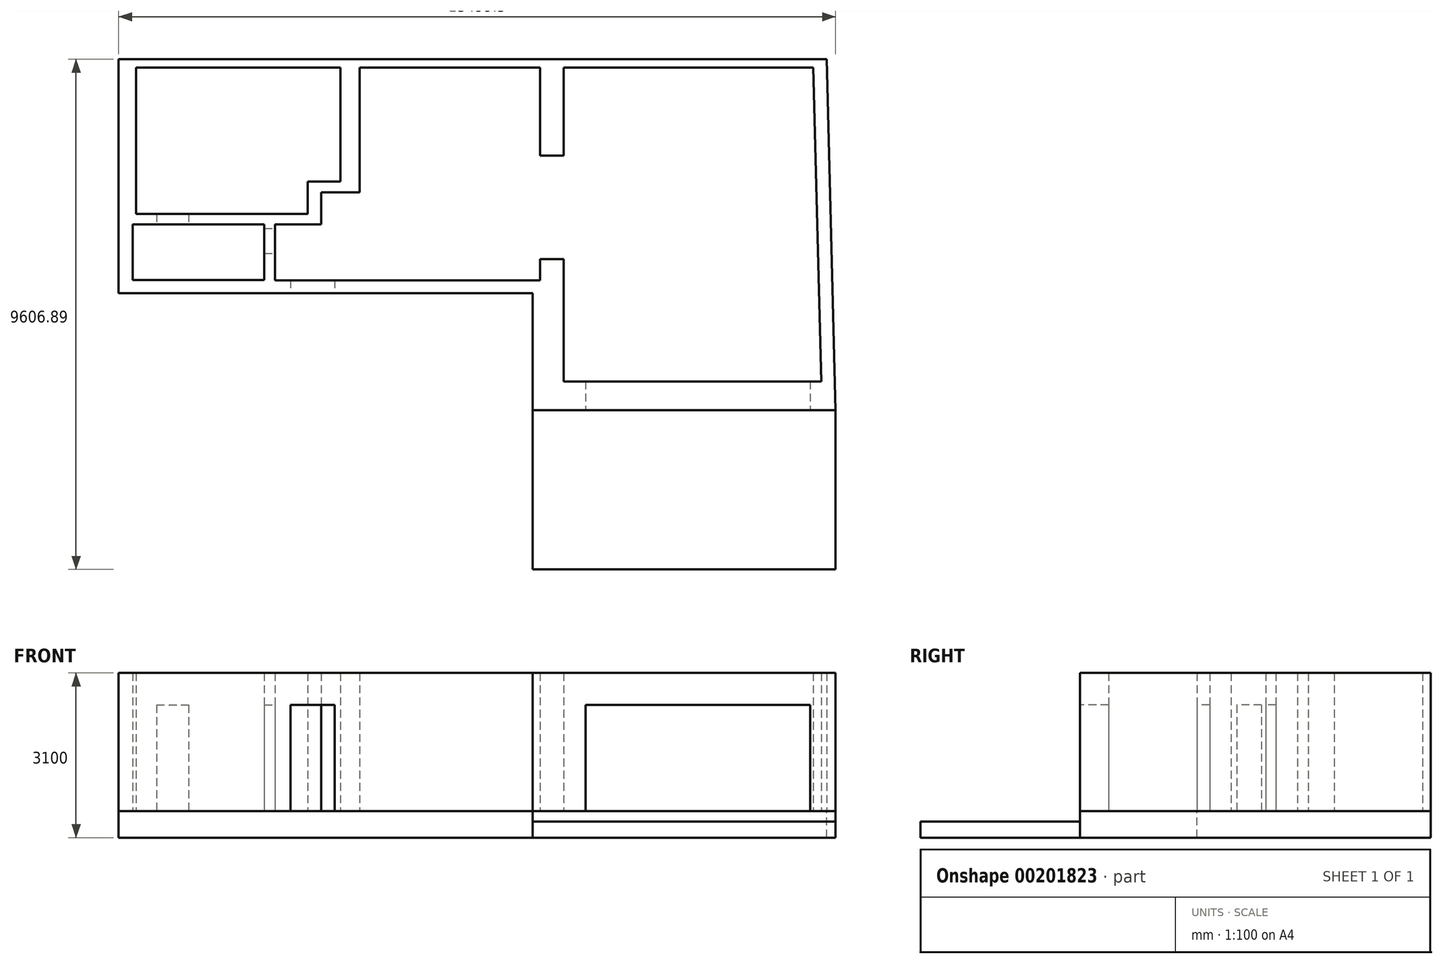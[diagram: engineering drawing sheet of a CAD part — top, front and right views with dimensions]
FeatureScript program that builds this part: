
annotation { "Feature Type Name" : "Feature", "Feature Type Description" : "" }
export const myFeature = defineFeature(function(context is Context, id is Id, definition is map)
    precondition{}
    {
        {
            var Q0;
            Q0=qCreatedBy(makeId("Top.planeOp"),FACE);
            var sketch = newSketch(context, id + "F0", { "sketchPlane" : qUnion([Q0])});
            skLineSegment(sketch, "E0", {"start": v(-2393.35, -759.16) * mm, "end": v(-2393.35, -518.36) * mm});
            skLineSegment(sketch, "E1", {"start": v(-2393.35, -518.36) * mm, "end": v(-2688.76, -518.36) * mm});
            skLineSegment(sketch, "E2", {"start": v(-2688.76, -518.36) * mm, "end": v(-2688.76, -9.52) * mm});
            skLineSegment(sketch, "E3", {"start": v(-2688.76, -9.52) * mm, "end": v(-2888.42, -9.52) * mm});
            skLineSegment(sketch, "E4", {"start": v(-2888.42, -9.52) * mm, "end": v(-2888.42, -513.76) * mm});
            skLineSegment(sketch, "E5", {"start": v(-2888.42, -513.76) * mm, "end": v(-5364.36, -513.76) * mm});
            skLineSegment(sketch, "E6", {"start": v(-5364.36, -513.76) * mm, "end": v(-5364.36, 536.6) * mm});
            skLineSegment(sketch, "E7", {"start": v(-5364.36, 536.6) * mm, "end": v(-4917.07, 536.6) * mm});
            skLineSegment(sketch, "E8", {"start": v(-4917.07, 536.6) * mm, "end": v(-4917.07, 728.5) * mm});
            skLineSegment(sketch, "E9", {"start": v(-4917.07, 728.5) * mm, "end": v(-5303.89, 728.5) * mm});
            skLineSegment(sketch, "E10", {"start": v(-5303.89, 728.5) * mm, "end": v(-5303.89, 3488.5) * mm});
            skLineSegment(sketch, "E11", {"start": v(-5303.89, 3488.5) * mm, "end": v(-1453.89, 3488.5) * mm});
            skLineSegment(sketch, "E12", {"start": v(-1453.89, 3488.5) * mm, "end": v(-1453.89, 1338.5) * mm});
            skLineSegment(sketch, "E13", {"start": v(-1453.89, 1338.5) * mm, "end": v(-2073.89, 1338.5) * mm});
            skLineSegment(sketch, "E14", {"start": v(-2073.89, 1338.5) * mm, "end": v(-2073.89, 728.5) * mm});
            skLineSegment(sketch, "E15", {"start": v(-2073.89, 728.5) * mm, "end": v(-4310.98, 728.5) * mm});
            skLineSegment(sketch, "E16", {"start": v(-4310.98, 728.5) * mm, "end": v(-4310.98, 536.6) * mm});
            skLineSegment(sketch, "E17", {"start": v(-4310.98, 536.6) * mm, "end": v(-2888.42, 536.6) * mm});
            skLineSegment(sketch, "E18", {"start": v(-2888.42, 536.6) * mm, "end": v(-2888.42, 458.15) * mm});
            skLineSegment(sketch, "E19", {"start": v(-2888.42, 458.15) * mm, "end": v(-2688.76, 458.15) * mm});
            skLineSegment(sketch, "E20", {"start": v(-2688.76, 458.15) * mm, "end": v(-2688.76, 536.6) * mm});
            skLineSegment(sketch, "E21", {"start": v(-2688.76, 536.6) * mm, "end": v(-1818.64, 536.6) * mm});
            skLineSegment(sketch, "E22", {"start": v(-1818.64, 536.6) * mm, "end": v(-1818.64, 1136.91) * mm});
            skLineSegment(sketch, "E23", {"start": v(-1818.64, 1136.91) * mm, "end": v(-1095.24, 1136.91) * mm});
            skLineSegment(sketch, "E24", {"start": v(-1095.24, 1136.91) * mm, "end": v(-1095.24, 3488.5) * mm});
            skLineSegment(sketch, "E25", {"start": v(-1095.24, 3488.5) * mm, "end": v(2304.76, 3488.5) * mm});
            skLineSegment(sketch, "E26", {"start": v(2304.76, 3488.5) * mm, "end": v(2304.76, 1828.5) * mm});
            skLineSegment(sketch, "E27", {"start": v(2304.76, 1828.5) * mm, "end": v(2749.76, 1828.5) * mm});
            skLineSegment(sketch, "E28", {"start": v(2749.76, 1828.5) * mm, "end": v(2749.76, 3488.5) * mm});
            skLineSegment(sketch, "E29", {"start": v(2749.76, 3488.5) * mm, "end": v(7449.76, 3488.5) * mm});
            skLineSegment(sketch, "E30", {"start": v(7449.76, 3488.5) * mm, "end": v(7599.76, -2422.42) * mm});
            skLineSegment(sketch, "E31", {"start": v(7599.76, -2422.42) * mm, "end": v(7390.63, -2422.42) * mm});
            skLineSegment(sketch, "E32", {"start": v(7390.63, -2422.42) * mm, "end": v(7390.63, -2963.9) * mm});
            skLineSegment(sketch, "E33", {"start": v(7390.63, -2963.9) * mm, "end": v(7867.99, -2963.9) * mm});
            skLineSegment(sketch, "E34", {"start": v(7700.33, 3642.99) * mm, "end": v(-5631.55, 3642.99) * mm});
            skLineSegment(sketch, "E35", {"start": v(-5631.55, 3642.99) * mm, "end": v(-5631.55, -759.16) * mm});
            skLineSegment(sketch, "E36", {"start": v(-5631.55, -759.16) * mm, "end": v(-2393.35, -759.16) * mm});
            skLineSegment(sketch, "E37", {"start": v(-1562.73, -759.16) * mm, "end": v(-1562.73, -518.36) * mm});
            skLineSegment(sketch, "E38", {"start": v(-1562.73, -518.36) * mm, "end": v(2304.76, -518.36) * mm});
            skLineSegment(sketch, "E39", {"start": v(2304.76, -518.36) * mm, "end": v(2304.76, -118.36) * mm});
            skLineSegment(sketch, "E40", {"start": v(2304.76, -118.36) * mm, "end": v(2749.76, -118.36) * mm});
            skLineSegment(sketch, "E41", {"start": v(2749.76, -118.36) * mm, "end": v(2749.76, -2422.42) * mm});
            skLineSegment(sketch, "E42", {"start": v(2749.76, -2422.42) * mm, "end": v(3164.2, -2422.42) * mm});
            skLineSegment(sketch, "E43", {"start": v(3164.2, -2422.42) * mm, "end": v(3164.2, -2963.9) * mm});
            skLineSegment(sketch, "E44", {"start": v(3164.2, -2963.9) * mm, "end": v(2166.9, -2963.9) * mm});
            skLineSegment(sketch, "E45", {"start": v(2166.9, -2963.9) * mm, "end": v(2166.9, -759.16) * mm});
            skLineSegment(sketch, "E46", {"start": v(2166.9, -759.16) * mm, "end": v(-1562.73, -759.16) * mm});
            skLineSegment(sketch, "E47", {"start": v(3164.2, -2422.42) * mm, "end": v(7390.63, -2422.42) * mm});
            skLineSegment(sketch, "E48", {"start": v(7390.63, -2963.9) * mm, "end": v(3164.2, -2963.9) * mm});
            skLineSegment(sketch, "E49", {"start": v(-2393.35, -518.36) * mm, "end": v(-1562.73, -518.36) * mm});
            skLineSegment(sketch, "E50", {"start": v(-1562.73, -759.16) * mm, "end": v(-2393.35, -759.16) * mm});
            skLineSegment(sketch, "E51", {"start": v(-2888.42, 458.15) * mm, "end": v(-2888.42, -9.52) * mm});
            skLineSegment(sketch, "E52", {"start": v(-2688.76, -9.52) * mm, "end": v(-2688.76, 458.15) * mm});
            skLineSegment(sketch, "E53", {"start": v(-4917.07, 728.5) * mm, "end": v(-4310.98, 728.5) * mm});
            skLineSegment(sketch, "E54", {"start": v(-4310.98, 536.6) * mm, "end": v(-4917.07, 536.6) * mm});
            skLineSegment(sketch, "E55", {"start": v(-1453.89, 3488.5) * mm, "end": v(-1095.24, 3488.5) * mm, "construction": true});
            skLineSegment(sketch, "E56", {"start": v(-2888.42, 536.6) * mm, "end": v(-2688.76, 536.6) * mm, "construction": true});
            skLineSegment(sketch, "E57.bottom", {"start": v(-1095.24, 1136.91) * mm, "end": v(-1494.07, 1136.91) * mm});
            skLineSegment(sketch, "E58", {"start": v(2749.76, -118.36) * mm, "end": v(2749.76, 1828.5) * mm, "construction": true});
            skLineSegment(sketch, "E59", {"start": v(7700.33, 3642.99) * mm, "end": v(7867.99, -2963.9) * mm});
            skSolve(sketch);
        }
        {
            var Q0;
            Q0=makeQuery(id+"F0.imprint","IMPRINT",FACE,{"disambiguationData":[TD([[makeQuery(id+"F0.imprint","IMPRINT",EDGE,{"derivedFrom":sQuery(id+"F0.wireOp",EDGE,"E0")}),1.0]])]});
            var Q1;
            Q1=makeQuery(id+"F0.imprint","IMPRINT",FACE,{"disambiguationData":[TD([[makeQuery(id+"F0.imprint","IMPRINT",EDGE,{"derivedFrom":sQuery(id+"F0.wireOp",EDGE,"E0")}),-1.0]])]});
            var Q2;
            Q2=makeQuery(id+"F0.imprint","IMPRINT",FACE,{"disambiguationData":[TD([[makeQuery(id+"F0.imprint","IMPRINT",EDGE,{"derivedFrom":sQuery(id+"F0.wireOp",EDGE,"E37")}),-1.0]])]});
            var Q3;
            Q3=makeQuery(id+"F0.imprint","IMPRINT",FACE,{"disambiguationData":[TD([[makeQuery(id+"F0.imprint","IMPRINT",EDGE,{"derivedFrom":sQuery(id+"F0.wireOp",EDGE,"E32")}),-1.0]])]});
            var Q4;
            Q4=makeQuery(id+"F0.imprint","IMPRINT",FACE,{"disambiguationData":[TD([[makeQuery(id+"F0.imprint","IMPRINT",EDGE,{"derivedFrom":sQuery(id+"F0.wireOp",EDGE,"E3")}),-1.0]])]});
            var Q5;
            Q5=makeQuery(id+"F0.imprint","IMPRINT",FACE,{"disambiguationData":[TD([[makeQuery(id+"F0.imprint","IMPRINT",EDGE,{"derivedFrom":sQuery(id+"F0.wireOp",EDGE,"E8")}),-1.0]])]});
            var Q6;
            Q6=makeQuery(id+"F0.imprint","IMPRINT",FACE,{"disambiguationData":[TD([[makeQuery(id+"F0.imprint","IMPRINT",EDGE,{"derivedFrom":sQuery(id+"F0.wireOp",EDGE,"E9")}),-1.0]])]});
            var Q7;
            Q7=makeQuery(id+"F0.imprint","IMPRINT",FACE,{"disambiguationData":[TD([[makeQuery(id+"F0.imprint","IMPRINT",EDGE,{"derivedFrom":sQuery(id+"F0.wireOp",EDGE,"E4")}),-1.0]])]});
            var Q8;
            Q8=makeQuery(id+"F0.imprint","IMPRINT",FACE,{"disambiguationData":[TD([[makeQuery(id+"F0.imprint","IMPRINT",EDGE,{"derivedFrom":sQuery(id+"F0.wireOp",EDGE,"E1")}),-1.0]])]});
            extrude(context, id + "F1", {"entities" : qUnion([Q0, Q1, Q2, Q3, Q4, Q5, Q6, Q7, Q8]), "oppositeDirection" : true, "depth" : 500 * mm});
        }
        {
            var Q0;
            Q0=makeQuery(id+"F0.imprint","IMPRINT",FACE,{"disambiguationData":[TD([[makeQuery(id+"F0.imprint","IMPRINT",EDGE,{"derivedFrom":sQuery(id+"F0.wireOp",EDGE,"E0")}),1.0]])]});
            var Q1;
            Q1=makeQuery(id+"F0.imprint","IMPRINT",FACE,{"disambiguationData":[TD([[makeQuery(id+"F0.imprint","IMPRINT",EDGE,{"derivedFrom":sQuery(id+"F0.wireOp",EDGE,"E37")}),-1.0]])]});
            extrude(context, id + "F2", {"entities" : qUnion([Q0, Q1]), "depth" : 2600 * mm});
        }
        {
            var Q0;
            Q0=makeQuery(id+"F1.opExtrude","CAP_FACE",FACE,{"disambiguationData":[OSD([sQuery(id+"F0.wireOp",EDGE,"E33"),sQuery(id+"F0.wireOp",EDGE,"nEtp4WkR-m3eL-wyIJ-Avfq-g6g80PU1rIS8"),sQuery(id+"F0.wireOp",EDGE,"E34"),sQuery(id+"F0.wireOp",EDGE,"E35"),sQuery(id+"F0.wireOp",EDGE,"E36"),sQuery(id+"F0.wireOp",EDGE,"E44"),sQuery(id+"F0.wireOp",EDGE,"E45"),sQuery(id+"F0.wireOp",EDGE,"E46"),sQuery(id+"F0.wireOp",EDGE,"E48"),sQuery(id+"F0.wireOp",EDGE,"E50")])],"isStart":true});
            cPlane(context, id + "F3", {"entities" : qUnion([Q0]), "cplaneType" : CPlaneType.OFFSET, "offset" : 2000 * mm, "width" : 150 * mm, "height" : 150 * mm});
        }
        {
            var Q0;
            Q0=qCreatedBy(id+"F3.planeOp",FACE);
            var sketch = newSketch(context, id + "F4", { "sketchPlane" : qUnion([Q0])});
            skLineSegment(sketch, "E60.bottom", {"start": v(-2393.35, -518.36) * mm, "end": v(-1562.73, -518.36) * mm});
            skLineSegment(sketch, "E60.top", {"start": v(-2393.35, -759.16) * mm, "end": v(-1562.73, -759.16) * mm});
            skLineSegment(sketch, "E60.left", {"start": v(-2393.35, -518.36) * mm, "end": v(-2393.35, -759.16) * mm});
            skLineSegment(sketch, "E60.right", {"start": v(-1562.73, -518.36) * mm, "end": v(-1562.73, -759.16) * mm});
            skLineSegment(sketch, "E61.bottom", {"start": v(-2888.42, 458.15) * mm, "end": v(-2688.76, 458.15) * mm});
            skLineSegment(sketch, "E61.top", {"start": v(-2888.42, -9.52) * mm, "end": v(-2688.76, -9.52) * mm});
            skLineSegment(sketch, "E61.left", {"start": v(-2888.42, 458.15) * mm, "end": v(-2888.42, -9.52) * mm});
            skLineSegment(sketch, "E61.right", {"start": v(-2688.76, 458.15) * mm, "end": v(-2688.76, -9.52) * mm});
            skLineSegment(sketch, "E62.bottom", {"start": v(-4917.07, 728.5) * mm, "end": v(-4310.98, 728.5) * mm});
            skLineSegment(sketch, "E62.top", {"start": v(-4917.07, 536.6) * mm, "end": v(-4310.98, 536.6) * mm});
            skLineSegment(sketch, "E62.left", {"start": v(-4917.07, 728.5) * mm, "end": v(-4917.07, 536.6) * mm});
            skLineSegment(sketch, "E62.right", {"start": v(-4310.98, 728.5) * mm, "end": v(-4310.98, 536.6) * mm});
            skLineSegment(sketch, "E63.bottom", {"start": v(3164.2, -2422.42) * mm, "end": v(7390.63, -2422.42) * mm});
            skLineSegment(sketch, "E63.top", {"start": v(3164.2, -2963.9) * mm, "end": v(7390.63, -2963.9) * mm});
            skLineSegment(sketch, "E63.left", {"start": v(3164.2, -2422.42) * mm, "end": v(3164.2, -2963.9) * mm});
            skLineSegment(sketch, "E63.right", {"start": v(7390.63, -2422.42) * mm, "end": v(7390.63, -2963.9) * mm});
            skSolve(sketch);
        }
        {
            var Q0;
            Q0=makeQuery(id+"F4.imprint","IMPRINT",FACE,{"disambiguationData":[TD([[makeQuery(id+"F4.imprint","IMPRINT",EDGE,{"derivedFrom":sQuery(id+"F4.wireOp",EDGE,"E60.bottom")}),-1.0]])]});
            var Q1;
            Q1=makeQuery(id+"F4.imprint","IMPRINT",FACE,{"disambiguationData":[TD([[makeQuery(id+"F4.imprint","IMPRINT",EDGE,{"derivedFrom":sQuery(id+"F4.wireOp",EDGE,"E62.bottom")}),-1.0]])]});
            var Q2;
            Q2=makeQuery(id+"F4.imprint","IMPRINT",FACE,{"disambiguationData":[TD([[makeQuery(id+"F4.imprint","IMPRINT",EDGE,{"derivedFrom":sQuery(id+"F4.wireOp",EDGE,"E61.bottom")}),-1.0]])]});
            var Q3;
            Q3=makeQuery(id+"F4.imprint","IMPRINT",FACE,{"disambiguationData":[TD([[makeQuery(id+"F4.imprint","IMPRINT",EDGE,{"derivedFrom":sQuery(id+"F4.wireOp",EDGE,"E63.bottom")}),-1.0]])]});
            var Q4;
            Q4=makeQuery(id+"F2.opExtrude","CAP_FACE",FACE,{"disambiguationData":[OSD([sQuery(id+"F0.wireOp",EDGE,"E37"),sQuery(id+"F0.wireOp",EDGE,"E38"),sQuery(id+"F0.wireOp",EDGE,"E39"),sQuery(id+"F0.wireOp",EDGE,"E40"),sQuery(id+"F0.wireOp",EDGE,"E41"),sQuery(id+"F0.wireOp",EDGE,"E42"),sQuery(id+"F0.wireOp",EDGE,"E43"),sQuery(id+"F0.wireOp",EDGE,"E44"),sQuery(id+"F0.wireOp",EDGE,"E45"),sQuery(id+"F0.wireOp",EDGE,"E46")])],"isStart":false});
            extrude(context, id + "F5", {"entities" : qUnion([Q0, Q1, Q2, Q3]), "operationType" : NewBodyOperationType.ADD, "endBound" : BoundingType.UP_TO_SURFACE, "endBoundEntityFace" : qUnion([Q4]), "depth" : 25 * mm});
        }
        {
            var Q0;
            {var subQ0=sQuery(id+"F0.wireOp",EDGE,"E44");var subQ1=sQuery(id+"F0.wireOp",EDGE,"E33");Q0=makeQuery(id+"F5.boolean.opBoolean","MERGE",FACE,{"derivedFrom":[makeQuery(id+"F2.boolean.opBoolean","MERGE",FACE,{"derivedFrom":[makeQuery(id+"F1.opExtrude","SWEPT_FACE",FACE,{"disambiguationData":[OSD([subQ1,subQ0,sQuery(id+"F0.wireOp",EDGE,"E48")])]}),makeQuery(id+"F2.opExtrude","SWEPT_FACE",FACE,{"disambiguationData":[OSD([subQ1])]}),makeQuery(id+"F2.opExtrude","SWEPT_FACE",FACE,{"disambiguationData":[OSD([subQ0])]})]}),makeQuery(id+"F5.opExtrude","SWEPT_FACE",FACE,{"disambiguationData":[OSD([sQuery(id+"F4.wireOp",EDGE,"E63.top")])]})]});}
            var sketch = newSketch(context, id + "F6", { "sketchPlane" : qUnion([Q0])});
            skLineSegment(sketch, "E64.bottom", {"start": v(2166.9, -500) * mm, "end": v(7867.99, -500) * mm});
            skLineSegment(sketch, "E64.top", {"start": v(2166.9, -200) * mm, "end": v(7867.99, -200) * mm});
            skLineSegment(sketch, "E64.left", {"start": v(2166.9, -500) * mm, "end": v(2166.9, -200) * mm});
            skLineSegment(sketch, "E64.right", {"start": v(7867.99, -500) * mm, "end": v(7867.99, -200) * mm});
            skSolve(sketch);
        }
        {
            var Q0;
            Q0=makeQuery(id+"F6.imprint","IMPRINT",FACE,{"disambiguationData":[TD([[makeQuery(id+"F6.imprint","IMPRINT",EDGE,{"derivedFrom":sQuery(id+"F6.wireOp",EDGE,"E64.bottom")}),1.0]])]});
            extrude(context, id + "F7", {"entities" : qUnion([Q0]), "depth" : 3000 * mm});
        }
    });
